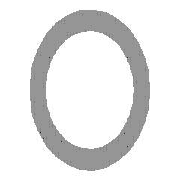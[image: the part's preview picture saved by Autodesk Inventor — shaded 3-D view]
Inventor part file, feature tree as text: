
AUTODESK INVENTOR PART (.ipt)
format: ipt  version: 2021 (Build 250183000, 183)  size: 110,592 bytes
history: native  units: mm (DEFAULTED — no unit token found)
features: other x4, sketch x3, extrude x1, plane x1
ambient origin geometry x8: Origin, YZ Plane, XZ Plane, XY Plane, X Axis, Y Axis, Z Axis, Center Point
bodies: Solid1 (feature_tree)
feature tree (9):
  parser-record x1  (decoder bookkeeping rows leaked as tree rows — omitted from the tree; the rows remain in map.json)
  other  "Driven Length"
  other  "Plano inicial"
  other  "Plano final"
  extrude  "Cuerpo"  Depth=2.8702mm
  sketch  "Boceto"  dims[d4=-0.0mm d5=570.0mm d6=90.0deg d7=570.0mm]
  sketch  "Sketch3"  dims[d0=26.67mm d1=2.8702mm]
  plane  "Work Plane3"
  sketch  "Sketch4"  dims[d2=570.0mm d3=0.0mm]
